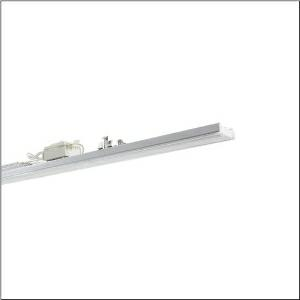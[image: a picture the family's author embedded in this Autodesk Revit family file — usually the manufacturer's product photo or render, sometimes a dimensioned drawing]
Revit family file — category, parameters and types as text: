
# Revit family: licross_r__11_recessed_mo_51te18mn495g_e68f
name_source: partatom
category: Lighting Fixtures
units: mm (PartAtom-declared; Revit-internal decimal feet)

## family parameters
Cut with Voids When Loaded = No
Host = Face
Light Source = No
Part Type = Normal
Room Calculation Point = No
Round Connector Dimension = Use Diameter
Shared = No

## types (1)
- --- (1 x LED, 9990 lm, 55.2 W, 4000K)
    Apparent Load = 55 VA
    CIE Flux Codes = 83 96 99 100 100
    Color Rendering = 80
    Color Temperature = 4000K
    Default Elevation = 1800 mm
    Description = Licross® 11 Recessed MO, luminaire insert, of sheet steel, galvanised, coil coated, white, length: 1.500mm, width: 66mm, height: 67mm, LED rated luminous flux: 9.990lm, light colour: 840, control gear: ON/OFF Multilumen, with plug, 3-pole, with phase selection, mains connection: 220..240V, AC, 50/60Hz, rated input power: 55W, internal wiring halogen-free, primary light control with lens, of plastic, primary optical cover: cover, of PMMA, light emission: direct distribution, primary light characteristic: symmetric, protection rating (complete): IP54, insulation class (complete): insulation class I (protective earthing), certification: CE, ENEC, VDE, UKCA, protection symbol: D if used in an environment with non-conductive dust loads with corresponding accessories, impact resistance: IK06, permissible ambient temperature for indoor applications: -35..+40°C, corresponds to IFS (International Featured Standards) requirements for safety and quality in the food industry, reducing of maximum allowable ambient temperature of 5°C with ceiling mounting, packaging unit: 1 piece
    Height = 58 mm
    Lamp = 1 x LED
    Lamp Light Flux = 9990 lm
    Lamp Power = 55.2 W
    Lamp count = 1
    Length = 1500 mm
    Luminous efficacy = 181 lm/W
    Manufacturer = Siteco
    ModVariant = No
    Model = 51TE18MN495G
    Mounting Place = Ceiling
    Mounting Type = Pendant
    Number of Poles = 1
    OnlyDefault = Yes
    Power Factor = 1
    Product Name = Licross® 11 Recessed MO
    Product group = luminaire insert | ceiling pendant
    ProductGroupID = 902
    Protection Class = Protection class I
    Protection Degree = IP 54
    RLX_Detail_Level = 1
    RLX_Emergency_Light_Flux = 0 lm
    RLX_Emergency_Type = 0
    RLX_Emergency_Type_DB = No
    RlxData = <blob elided: 22153 chars, md5=152cfd0c>
    Socket = socket
    Standby Power = 0 W
    System Light Flux = 9990 lm
    System Power = 55 W
    Type Comments = factory setting: luminous flux: 100 % | (A | C | E) | 126 mA
    Type Image = l_1296930.jpg
    URL = http://relux.com
    VarID = @adj_106149
    Voltage = 0 V
    Weight = 0.00 kg
    Width = 66 mm

## geometry (parser evidence)
native form markers: Blend x4, Sweep x11
no freeform markers — native parametric forms only
